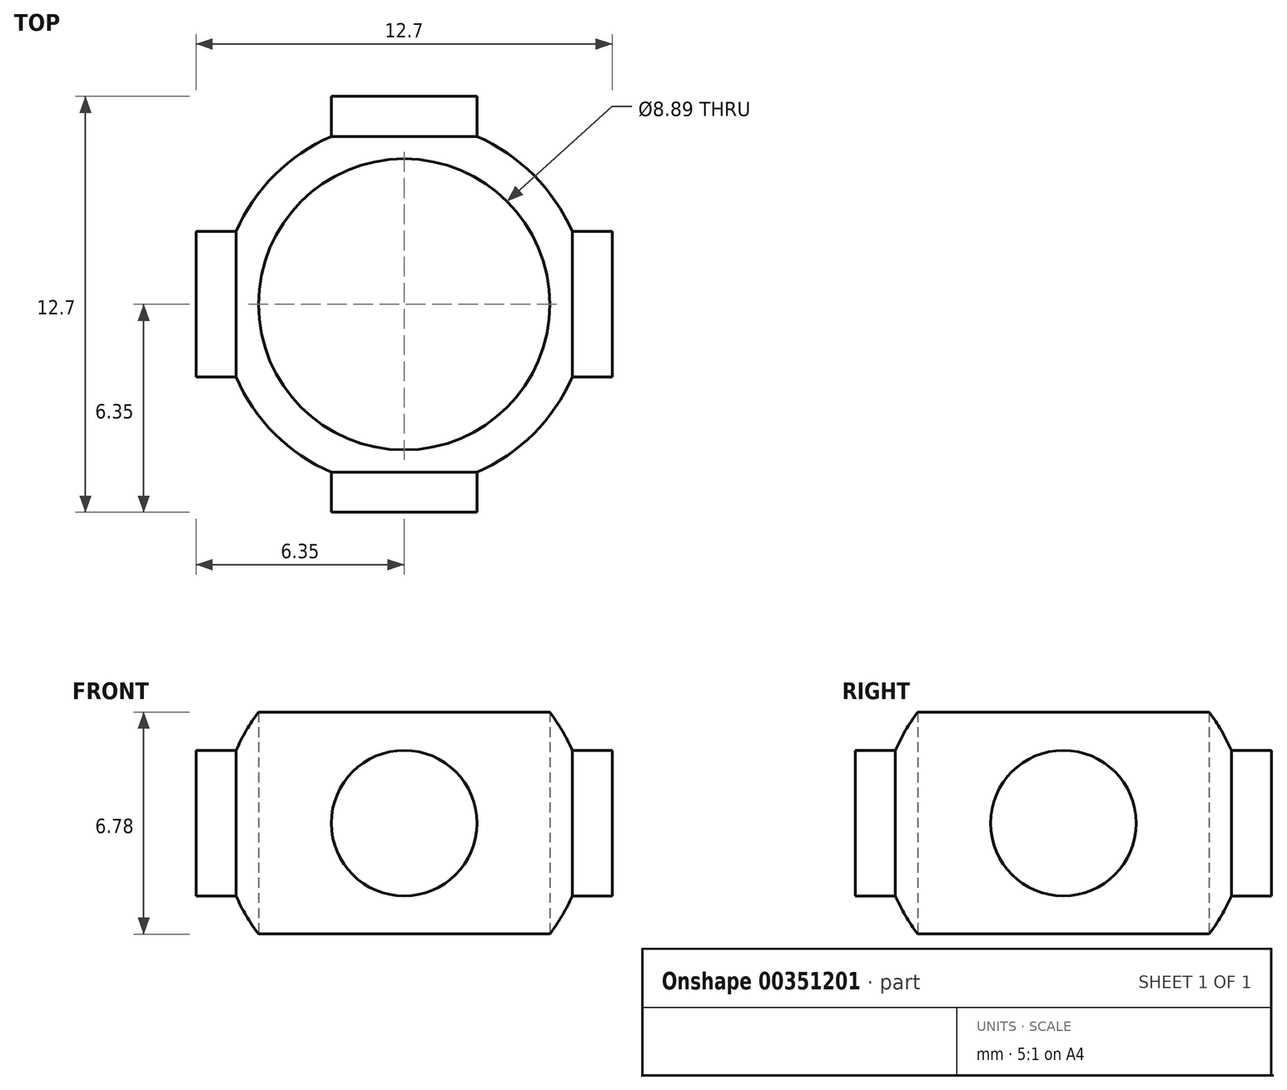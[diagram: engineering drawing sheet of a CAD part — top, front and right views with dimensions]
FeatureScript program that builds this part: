
annotation { "Feature Type Name" : "Feature", "Feature Type Description" : "" }
export const myFeature = defineFeature(function(context is Context, id is Id, definition is map)
    precondition{}
    {
        {
            var Q0;
            Q0=qCreatedBy(makeId("Right.planeOp"),FACE);
            var sketch = newSketch(context, id + "F0", { "sketchPlane" : qUnion([Q0])});
            skCircle(sketch, "E0", {"center": v(0, 0) * mm, "radius": 2.22 * mm});
            skSolve(sketch);
        }
        {
            var Q0;
            Q0=qCreatedBy(makeId("Front.planeOp"),FACE);
            var sketch = newSketch(context, id + "F1", { "sketchPlane" : qUnion([Q0])});
            skCircle(sketch, "E1", {"center": v(0, 0) * mm, "radius": 2.22 * mm});
            skSolve(sketch);
        }
        {
            var Q0;
            Q0=qCreatedBy(makeId("Right.planeOp"),FACE);
            var sketch = newSketch(context, id + "F2", { "sketchPlane" : qUnion([Q0])});
            skArc(sketch, "E2", {"start": v(0, -5.59) * mm, "mid": v(5.59, 0) * mm, "end": v(0, 5.59) * mm});
            skLineSegment(sketch, "E3", {"start": v(0, 16.65) * mm, "end": v(0, -18.6) * mm, "construction": true});
            skLineSegment(sketch, "E4", {"start": v(0, 5.59) * mm, "end": v(0, -5.59) * mm});
            skSolve(sketch);
        }
        {
            var Q0;
            Q0 = qSketchRegion(id + "F0", true);
            extrude(context, id + "F3", {"entities" : qUnion([Q0]), "endBound" : BoundingType.SYMMETRIC, "depth" : 12.7 * mm});
        }
        {
            var Q0;
            Q0 = qSketchRegion(id + "F1", true);
            extrude(context, id + "F4", {"entities" : qUnion([Q0]), "operationType" : NewBodyOperationType.ADD, "endBound" : BoundingType.SYMMETRIC, "depth" : 12.7 * mm});
        }
        {
            var Q0;
            Q0=makeQuery(id+"F2.imprint","IMPRINT",FACE,{"disambiguationData":[TD([[makeQuery(id+"F2.imprint","IMPRINT",EDGE,{"derivedFrom":sQuery(id+"F2.wireOp",EDGE,"E2")}),1.0]])]});
            var Q1;
            Q1=sQuery(id+"F2.wireOp",EDGE,"E3");
            revolve(context, id + "F5", {"operationType" : NewBodyOperationType.ADD, "entities" : qUnion([Q0]), "axis" : qUnion([Q1]), "revolveType" : RevolveType.FULL});
        }
        {
            var Q0;
            Q0=qCreatedBy(makeId("Top.planeOp"),FACE);
            var sketch = newSketch(context, id + "F6", { "sketchPlane" : qUnion([Q0])});
            skCircle(sketch, "E5", {"center": v(0, 0) * mm, "radius": 4.45 * mm});
            skSolve(sketch);
        }
        {
            var Q0;
            Q0 = qSketchRegion(id + "F6", true);
            extrude(context, id + "F7", {"entities" : qUnion([Q0]), "operationType" : NewBodyOperationType.REMOVE, "endBound" : BoundingType.SYMMETRIC, "depth" : 25.4 * mm});
        }
    });
